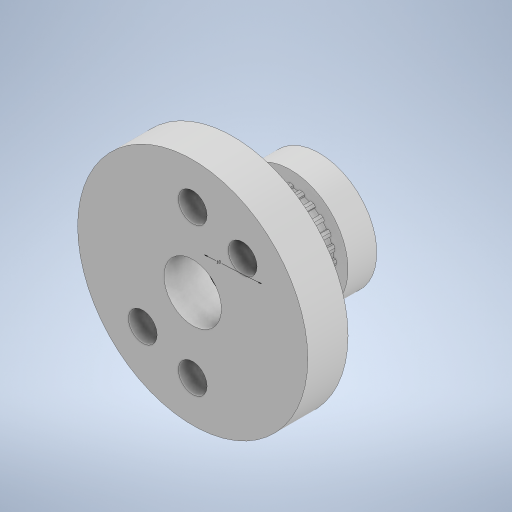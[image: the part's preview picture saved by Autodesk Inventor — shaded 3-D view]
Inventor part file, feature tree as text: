
AUTODESK INVENTOR PART (.ipt)
format: ipt  version: 2023.2 (Build 272271000, 271)  size: 441,344 bytes
history: native  units: mm
features: sketch x8, extrude x5, projected_geometry x2
ambient origin geometry x8: Origin, YZ Plane, XZ Plane, XY Plane, X Axis, Y Axis, Z Axis, Center Point
bodies: Solid1 (feature_tree)
feature tree (15):
  extrude  "Extrusion1"  Depth=10.0mm
  extrude  "Extrusion2"  Depth=12.85mm
  extrude  "Extrusion4"  Depth=12.85mm
  sketch  "Sketch6"  dims[d8=5.0mm d9=5.0mm d10=0.0mm]
  sketch  "Sketch7"  dims[d15=90.0deg d17=8.290314mm]
  extrude  "Extrusion5"  Depth=5.0mm TaperAngle=0.0deg
  extrude  "Extrusion6"  Depth=8.290314mm
  sketch  "Sketch10"  dims[d21=23.125613mm d22=5.0mm d23=12.85mm d24=5.0mm d25=7.417649mm d34=15.0mm d35=10.0mm d36=10.0mm d37=0.0mm d38=10.0mm d39=0.5mm d40=0.5mm d41=75.0deg d42=0.5mm d43=240.0mm d45=360.0deg d47=10.0mm d48=0.0mm d49=20.0mm d50=5.0mm d51=0.0mm d52=2.0mm d53=0.0mm]
  sketch  "Sketch1"  dims[d0=40.0mm d1=10.0mm]
  sketch  "Sketch2"  dims[d2=5.0mm d3=0.0mm d4=12.85mm]
  sketch  "Sketch5"  dims[d5=5.0mm d6=12.85mm]
  projected_geometry  "Projected Loop1"
  projected_geometry  "Projected Loop2"
  sketch  "Sketch8"  dims[d18=7.417649mm]
  sketch  "Sketch9"  dims[d20=12.85mm]
